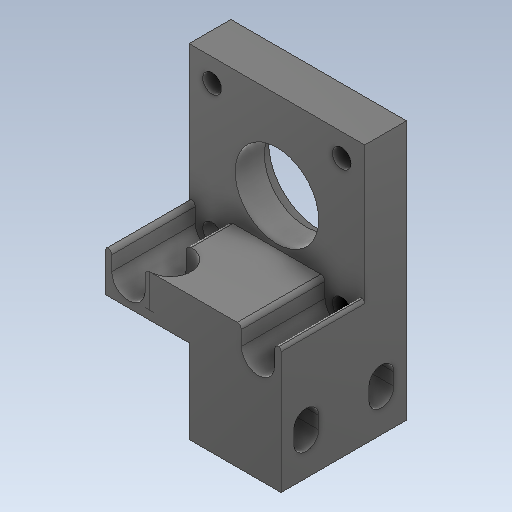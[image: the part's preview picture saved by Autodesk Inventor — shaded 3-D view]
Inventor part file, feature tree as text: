
AUTODESK INVENTOR PART (.ipt)
format: ipt  version: 2020 (Build 240168000, 168)  size: 285,184 bytes
history: native  units: mm
features: sketch x8, extrude x7, fillet x1, hole x1
ambient origin geometry x8: Origin, YZ Plane, XZ Plane, XY Plane, X Axis, Y Axis, Z Axis, Center Point
bodies: Solid1 (feature_tree)
feature tree (17):
  extrude  "Extrusion1"  Depth=42.0mm
  extrude  "Extrusion2"  Depth=10.0mm
  extrude  "Extrusion3"  TaperAngle=0.0deg  [1 undecoded]
  extrude  "Extrusion4"  Depth=21.0mm
  extrude  "Extrusion5"  Depth=3.0mm TaperAngle=0.0deg
  extrude  "Extrusion6"  Depth=5.5mm
  fillet  "Fillet1"  Radius=5.5mm
  extrude  "Extrusion7"  Depth=31.0mm
  hole  "Hole2"  [1 undecoded]
  sketch  "Sketch1"  dims[d0=62.0mm d1=42.0mm]
  sketch  "Sketch2"  dims[d2=10.0mm d3=0.0mm d4=20.0mm]
  sketch  "Sketch3"  dims[d6=20.0mm d7=0.0mm d8=0.0mm]
  sketch  "Sketch4"  dims[d9=21.0mm d10=21.0mm]
  sketch  "Sketch5"  dims[d11=24.0mm d12=3.0mm d13=0.0mm]
  sketch  "Sketch6"  dims[d14=4.5mm d15=5.5mm d16=5.5mm]
  sketch  "Sketch8"  dims[d17=31.0mm d18=31.0mm]
  sketch  "Sketch9"  dims[d19=15.5mm d20=15.5mm d21=20.0mm d22=0.0mm d23=0.0mm d24=10.0mm d25=20.0mm d26=0.0mm d27=8.0mm d28=15.0mm d29=0.0mm d30=1.0mm d44=0.0mm d45=0.0mm d47=5.0mm d48=5.0mm d49=6.0mm d50=10.0mm d51=8.0mm d52=90.0deg d53=8.0mm d54=20.594885mm d55=10.5mm d56=3.0mm d57=6.0mm d58=10.0mm d59=6.0mm d60=6.0mm d61=14.3117mm d62=0.75mm d63=20.594885mm d64=0.0625mm d65=0.75mm d66=0.375mm]
note: 2 required parameter values undecoded (feature->parameter linkage not recoverable at this tier; creation-order binding heuristic only, values carry confidence <= 0.55)
